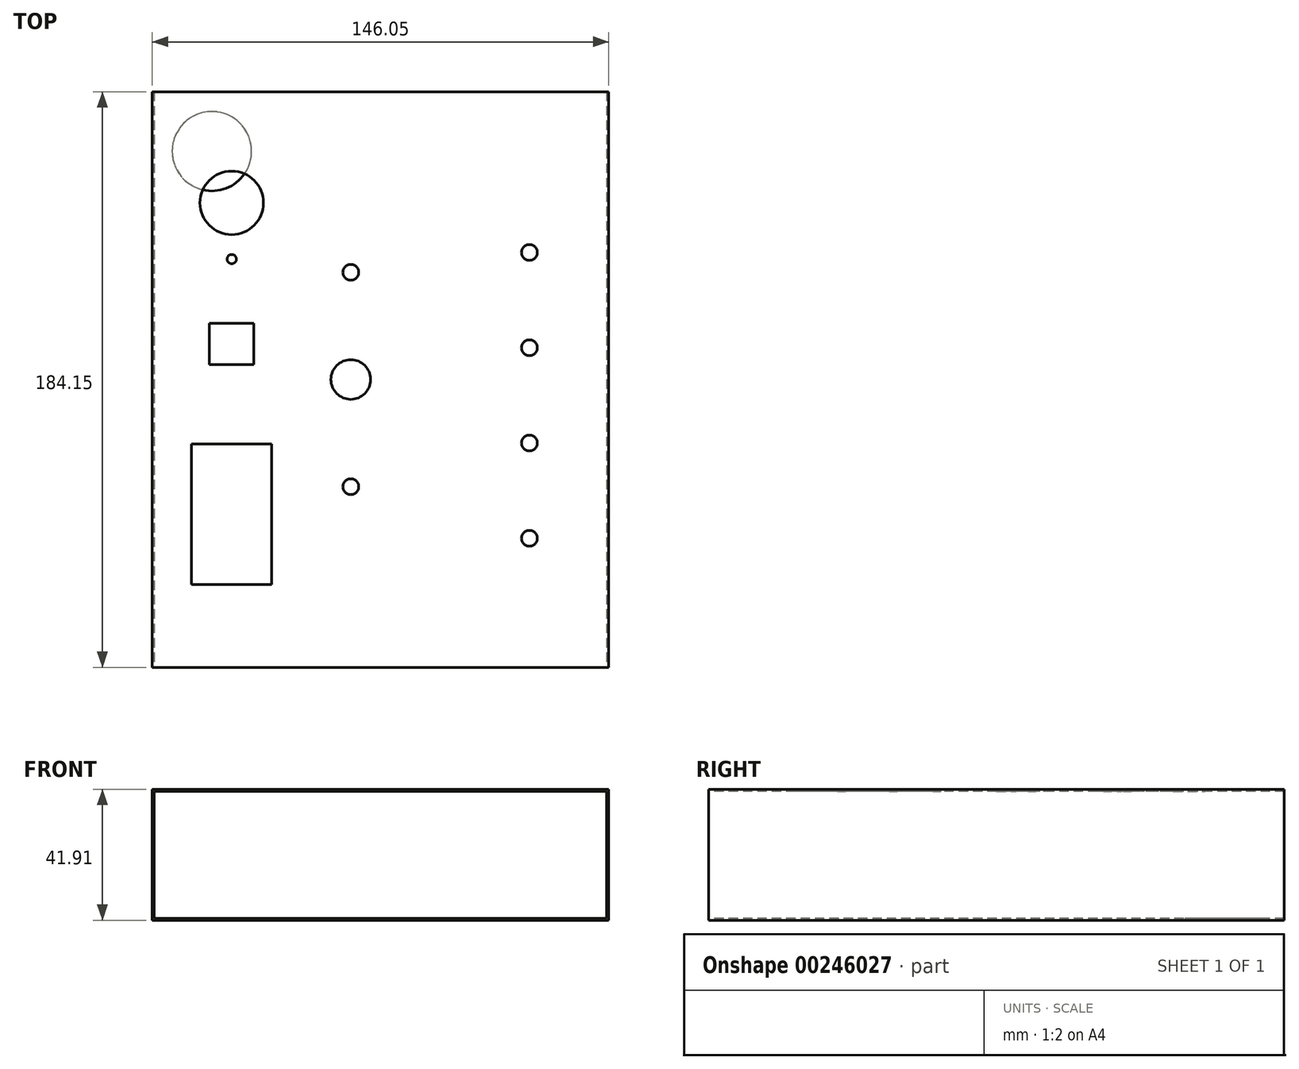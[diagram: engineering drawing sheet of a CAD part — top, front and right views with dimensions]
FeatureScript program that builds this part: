
annotation { "Feature Type Name" : "Feature", "Feature Type Description" : "" }
export const myFeature = defineFeature(function(context is Context, id is Id, definition is map)
    precondition{}
    {
        {
            var Q0;
            Q0=qCreatedBy(makeId("Front.planeOp"),FACE);
            var sketch = newSketch(context, id + "F0", { "sketchPlane" : qUnion([Q0])});
            skLineSegment(sketch, "E0.bottom", {"start": v(0, 0) * mm, "end": v(146.05, 0) * mm});
            skLineSegment(sketch, "E0.top", {"start": v(0, 41.91) * mm, "end": v(146.05, 41.91) * mm});
            skLineSegment(sketch, "E0.left", {"start": v(0, 0) * mm, "end": v(0, 41.91) * mm});
            skLineSegment(sketch, "E0.right", {"start": v(146.05, 0) * mm, "end": v(146.05, 41.91) * mm});
            skLineSegment(sketch, "E1.bottom", {"start": v(0.63, 0.64) * mm, "end": v(145.42, 0.64) * mm});
            skLineSegment(sketch, "E1.top", {"start": v(0.63, 41.27) * mm, "end": v(145.42, 41.27) * mm});
            skLineSegment(sketch, "E1.left", {"start": v(0.64, 0.64) * mm, "end": v(0.63, 41.27) * mm});
            skLineSegment(sketch, "E1.right", {"start": v(145.42, 0.64) * mm, "end": v(145.42, 41.27) * mm});
            skSolve(sketch);
        }
        {
            var Q0;
            Q0=makeQuery(id+"F0.imprint","IMPRINT",FACE,{"disambiguationData":[TD([[makeQuery(id+"F0.imprint","IMPRINT",EDGE,{"derivedFrom":sQuery(id+"F0.wireOp",EDGE,"E0.bottom")}),1.0]])]});
            extrude(context, id + "F1", {"entities" : qUnion([Q0]), "oppositeDirection" : true, "depth" : 184.15 * mm});
        }
        {
            var Q0;
            Q0=makeQuery(id+"F1.opExtrude","SWEPT_FACE",FACE,{"disambiguationData":[OSD([sQuery(id+"F0.wireOp",EDGE,"E0.bottom")])]});
            var sketch = newSketch(context, id + "F2", { "sketchPlane" : qUnion([Q0])});
            skCircle(sketch, "E2", {"center": v(19.05, -165.1) * mm, "radius": 12.7 * mm});
            skSolve(sketch);
        }
        {
            var Q0;
            Q0=makeQuery(id+"F2.imprint","IMPRINT",FACE,{"disambiguationData":[TD([[makeQuery(id+"F2.imprint","IMPRINT",EDGE,{"derivedFrom":sQuery(id+"F2.wireOp",EDGE,"E2")}),1.0]])]});
            var Q1;
            Q1=makeQuery(id+"F1.opExtrude","SWEPT_FACE",FACE,{"disambiguationData":[OSD([sQuery(id+"F0.wireOp",EDGE,"E1.bottom")])]});
            extrude(context, id + "F3", {"entities" : qUnion([Q0]), "operationType" : NewBodyOperationType.REMOVE, "endBound" : BoundingType.UP_TO_SURFACE, "oppositeDirection" : true, "endBoundEntityFace" : qUnion([Q1]), "depth" : 25.4 * mm});
        }
        {
            var Q0;
            Q0=makeQuery(id+"F1.opExtrude","SWEPT_FACE",FACE,{"disambiguationData":[OSD([sQuery(id+"F0.wireOp",EDGE,"E0.top")])]});
            var sketch = newSketch(context, id + "F4", { "sketchPlane" : qUnion([Q0])});
            skLineSegment(sketch, "E3", {"start": v(25.4, 0) * mm, "end": v(25.4, 184.15) * mm, "construction": true});
            skCircle(sketch, "E4", {"center": v(25.4, 148.6) * mm, "radius": 10.16 * mm});
            skCircle(sketch, "E5", {"center": v(25.4, 130.6) * mm, "radius": 1.49 * mm});
            skLineSegment(sketch, "E6.bottom", {"start": v(18.29, 110.06) * mm, "end": v(32.51, 110.06) * mm});
            skLineSegment(sketch, "E6.top", {"start": v(18.29, 96.85) * mm, "end": v(32.51, 96.85) * mm});
            skLineSegment(sketch, "E6.left", {"start": v(18.29, 110.06) * mm, "end": v(18.29, 96.85) * mm});
            skLineSegment(sketch, "E6.right", {"start": v(32.51, 110.06) * mm, "end": v(32.51, 96.85) * mm});
            skPoint(sketch, "E6.middle", {"position": v(25.4, 103.45) * mm});
            skLineSegment(sketch, "E7.bottom", {"start": v(12.57, 71.45) * mm, "end": v(38.23, 71.45) * mm});
            skLineSegment(sketch, "E7.top", {"start": v(12.57, 26.5) * mm, "end": v(38.23, 26.5) * mm});
            skLineSegment(sketch, "E7.left", {"start": v(12.57, 71.45) * mm, "end": v(12.57, 26.5) * mm});
            skLineSegment(sketch, "E7.right", {"start": v(38.23, 71.45) * mm, "end": v(38.23, 26.5) * mm});
            skPoint(sketch, "E7.middle", {"position": v(25.4, 48.97) * mm});
            skLineSegment(sketch, "E8", {"start": v(63.5, 0) * mm, "end": v(63.5, 184.15) * mm, "construction": true});
            skCircle(sketch, "E9", {"center": v(63.5, 92.08) * mm, "radius": 6.35 * mm});
            skLineSegment(sketch, "E10", {"start": v(120.65, 0) * mm, "end": v(120.65, 184.15) * mm, "construction": true});
            skCircle(sketch, "E11", {"center": v(120.65, 102.23) * mm, "radius": 2.54 * mm});
            skCircle(sketch, "E12", {"center": v(120.65, 71.75) * mm, "radius": 2.54 * mm});
            skCircle(sketch, "E13", {"center": v(120.65, 41.27) * mm, "radius": 2.54 * mm});
            skCircle(sketch, "E14", {"center": v(120.65, 132.71) * mm, "radius": 2.54 * mm});
            skCircle(sketch, "E15", {"center": v(63.5, 57.79) * mm, "radius": 2.54 * mm});
            skCircle(sketch, "E16", {"center": v(63.5, 126.37) * mm, "radius": 2.54 * mm});
            skSolve(sketch);
        }
        {
            var Q0;
            Q0=makeQuery(id+"F4.imprint","IMPRINT",FACE,{"disambiguationData":[TD([[makeQuery(id+"F4.imprint","IMPRINT",EDGE,{"derivedFrom":sQuery(id+"F4.wireOp",EDGE,"E7.bottom")}),-1.0]])]});
            var Q1;
            Q1=makeQuery(id+"F4.imprint","IMPRINT",FACE,{"disambiguationData":[TD([[makeQuery(id+"F4.imprint","IMPRINT",EDGE,{"derivedFrom":sQuery(id+"F4.wireOp",EDGE,"E6.bottom")}),-1.0]])]});
            var Q2;
            Q2=makeQuery(id+"F4.imprint","IMPRINT",FACE,{"disambiguationData":[TD([[makeQuery(id+"F4.imprint","IMPRINT",EDGE,{"derivedFrom":sQuery(id+"F4.wireOp",EDGE,"E4")}),1.0]])]});
            var Q3;
            Q3=makeQuery(id+"F4.imprint","IMPRINT",FACE,{"disambiguationData":[TD([[makeQuery(id+"F4.imprint","IMPRINT",EDGE,{"derivedFrom":sQuery(id+"F4.wireOp",EDGE,"E9")}),1.0]])]});
            var Q4;
            Q4=makeQuery(id+"F4.imprint","IMPRINT",FACE,{"disambiguationData":[TD([[makeQuery(id+"F4.imprint","IMPRINT",EDGE,{"derivedFrom":sQuery(id+"F4.wireOp",EDGE,"E15")}),1.0]])]});
            var Q5;
            Q5=makeQuery(id+"F4.imprint","IMPRINT",FACE,{"disambiguationData":[TD([[makeQuery(id+"F4.imprint","IMPRINT",EDGE,{"derivedFrom":sQuery(id+"F4.wireOp",EDGE,"E12")}),1.0]])]});
            var Q6;
            Q6=makeQuery(id+"F4.imprint","IMPRINT",FACE,{"disambiguationData":[TD([[makeQuery(id+"F4.imprint","IMPRINT",EDGE,{"derivedFrom":sQuery(id+"F4.wireOp",EDGE,"E14")}),1.0]])]});
            var Q7;
            Q7=makeQuery(id+"F1.opExtrude","SWEPT_FACE",FACE,{"disambiguationData":[OSD([sQuery(id+"F0.wireOp",EDGE,"E1.top")])]});
            extrude(context, id + "F5", {"entities" : qUnion([Q0, Q1, Q2, Q3, Q4, Q5, Q6]), "operationType" : NewBodyOperationType.REMOVE, "endBound" : BoundingType.UP_TO_SURFACE, "oppositeDirection" : true, "endBoundEntityFace" : qUnion([Q7]), "depth" : 25.4 * mm});
        }
        {
            var Q0;
            Q0=makeQuery(id+"F4.imprint","IMPRINT",FACE,{"disambiguationData":[TD([[makeQuery(id+"F4.imprint","IMPRINT",EDGE,{"derivedFrom":sQuery(id+"F4.wireOp",EDGE,"E5")}),1.0]])]});
            var Q1;
            Q1=makeQuery(id+"F4.imprint","IMPRINT",FACE,{"disambiguationData":[TD([[makeQuery(id+"F4.imprint","IMPRINT",EDGE,{"derivedFrom":sQuery(id+"F4.wireOp",EDGE,"E16")}),1.0]])]});
            var Q2;
            Q2=makeQuery(id+"F4.imprint","IMPRINT",FACE,{"disambiguationData":[TD([[makeQuery(id+"F4.imprint","IMPRINT",EDGE,{"derivedFrom":sQuery(id+"F4.wireOp",EDGE,"E11")}),1.0]])]});
            var Q3;
            Q3=makeQuery(id+"F4.imprint","IMPRINT",FACE,{"disambiguationData":[TD([[makeQuery(id+"F4.imprint","IMPRINT",EDGE,{"derivedFrom":sQuery(id+"F4.wireOp",EDGE,"E13")}),1.0]])]});
            var Q4;
            Q4=makeQuery(id+"F1.opExtrude","SWEPT_FACE",FACE,{"disambiguationData":[OSD([sQuery(id+"F0.wireOp",EDGE,"E1.top")])]});
            extrude(context, id + "F6", {"entities" : qUnion([Q0, Q1, Q2, Q3]), "operationType" : NewBodyOperationType.REMOVE, "endBound" : BoundingType.UP_TO_SURFACE, "oppositeDirection" : true, "endBoundEntityFace" : qUnion([Q4]), "depth" : 25.4 * mm});
        }
    });
